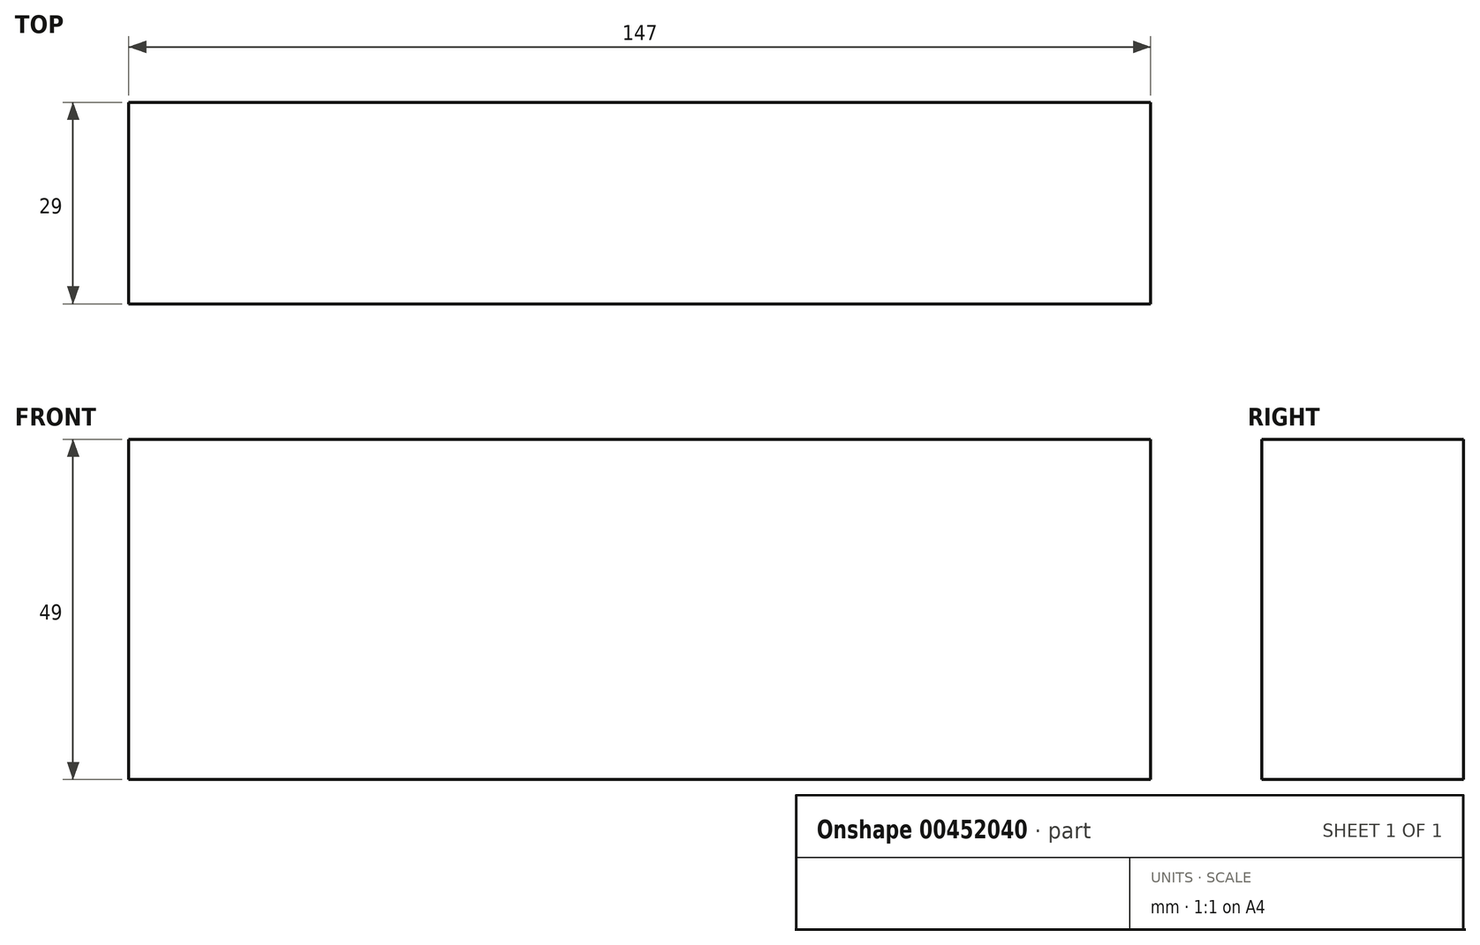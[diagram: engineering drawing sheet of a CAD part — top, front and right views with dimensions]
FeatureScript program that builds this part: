
annotation { "Feature Type Name" : "Feature", "Feature Type Description" : "" }
export const myFeature = defineFeature(function(context is Context, id is Id, definition is map)
    precondition{}
    {
        {
            var Q0;
            Q0=qCreatedBy(makeId("Top.planeOp"),FACE);
            var sketch = newSketch(context, id + "F0", { "sketchPlane" : qUnion([Q0])});
            skLineSegment(sketch, "E0.bottom", {"start": v(0, 0) * mm, "end": v(147, 0) * mm});
            skLineSegment(sketch, "E0.top", {"start": v(0, -29) * mm, "end": v(147, -29) * mm});
            skLineSegment(sketch, "E0.left", {"start": v(0, 0) * mm, "end": v(0, -29) * mm});
            skLineSegment(sketch, "E0.right", {"start": v(147, 0) * mm, "end": v(147, -29) * mm});
            skSolve(sketch);
        }
        {
            var Q0;
            Q0 = qSketchRegion(id + "F0", true);
            extrude(context, id + "F1", {"entities" : qUnion([Q0]), "depth" : 49 * mm});
        }
    });
